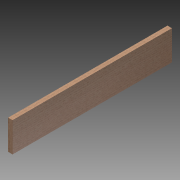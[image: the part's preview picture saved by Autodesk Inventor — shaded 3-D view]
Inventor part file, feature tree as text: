
AUTODESK INVENTOR PART (.ipt)
format: ipt  version: 2014 SP1 (Build 180222100, 222)  size: 95,232 bytes
history: native  units: in
note: dims shown in document units (in); Inventor stores cm internally (conversion verified against a paired STEP export)
features: extrude x1, sketch x1
ambient origin geometry x8: Origin, YZ Plane, XZ Plane, XY Plane, X Axis, Y Axis, Z Axis, Center Point
bodies: Solid1 (feature_tree)
feature tree (2):
  extrude  "Extrusion1"  Depth=0.75in
  sketch  "Sketch1"  dims[d0=5.0in d1=0.75in d2=26.875in d3=0.0in]
